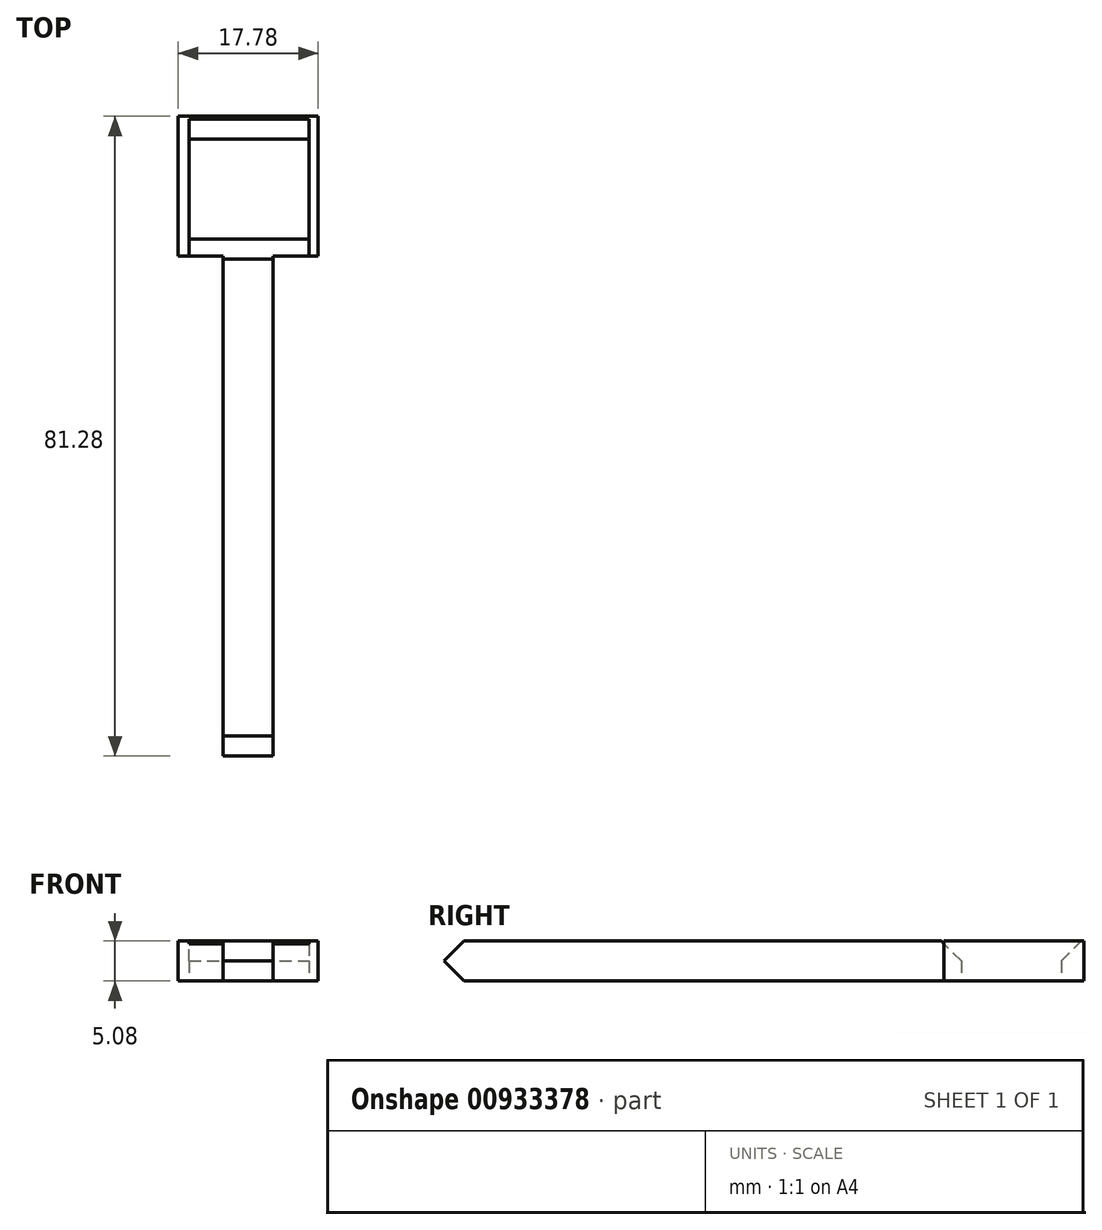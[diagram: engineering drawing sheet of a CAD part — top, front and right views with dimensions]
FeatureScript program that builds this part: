
annotation { "Feature Type Name" : "Feature", "Feature Type Description" : "" }
export const myFeature = defineFeature(function(context is Context, id is Id, definition is map)
    precondition{}
    {
        {
            var Q0;
            Q0=qCreatedBy(makeId("Top.planeOp"),FACE);
            var sketch = newSketch(context, id + "F0", { "sketchPlane" : qUnion([Q0])});
            skLineSegment(sketch, "E0.bottom", {"start": v(-37.97, 21.15) * mm, "end": v(-31.62, 21.15) * mm});
            skLineSegment(sketch, "E0.top", {"start": v(-37.97, -42.35) * mm, "end": v(-31.62, -42.35) * mm});
            skLineSegment(sketch, "E0.left", {"start": v(-37.97, 21.15) * mm, "end": v(-37.97, -42.35) * mm});
            skLineSegment(sketch, "E0.right", {"start": v(-31.62, 21.15) * mm, "end": v(-31.62, -42.35) * mm});
            skLineSegment(sketch, "E1", {"start": v(-34.8, 21.15) * mm, "end": v(-43.69, 21.15) * mm});
            skLineSegment(sketch, "E2", {"start": v(-34.8, 21.15) * mm, "end": v(-25.9, 21.15) * mm});
            skLineSegment(sketch, "E3", {"start": v(-43.69, 21.15) * mm, "end": v(-43.69, 38.93) * mm});
            skLineSegment(sketch, "E4", {"start": v(-43.69, 38.93) * mm, "end": v(-25.9, 38.93) * mm});
            skLineSegment(sketch, "E5", {"start": v(-25.9, 38.93) * mm, "end": v(-25.9, 21.15) * mm});
            skLineSegment(sketch, "E6.bottom", {"start": v(-42.3, 23.34) * mm, "end": v(-27.05, 23.34) * mm});
            skLineSegment(sketch, "E6.top", {"start": v(-42.3, 36.04) * mm, "end": v(-27.05, 36.04) * mm});
            skLineSegment(sketch, "E6.left", {"start": v(-42.3, 23.34) * mm, "end": v(-42.3, 36.04) * mm});
            skLineSegment(sketch, "E6.right", {"start": v(-27.05, 23.34) * mm, "end": v(-27.05, 36.04) * mm});
            skSolve(sketch);
        }
        {
            var Q0;
            {var subQ0=sQuery(id+"F0.wireOp",EDGE,"jYGAuy7J-s2xA-IOac-4ksF-dyn8kirWFf4m.top");Q0=makeQuery(id+"F0.imprint","IMPRINT",FACE,{"disambiguationData":[TD([[makeQuery(id+"F0.imprint","IMPRINT",EDGE,{"derivedFrom":subQ0}),1.0]])]});}
            var Q1;
            {var subQ1=sQuery(id+"F0.wireOp",EDGE,"jYGAuy7J-s2xA-IOac-4ksF-dyn8kirWFf4m.bottom");Q1=makeQuery(id+"F0.imprint","IMPRINT",FACE,{"disambiguationData":[TD([[makeQuery(id+"F0.imprint","IMPRINT",EDGE,{"derivedFrom":subQ1}),-1.0]])]});}
            var Q2;
            {var subQ0=sQuery(id+"F0.wireOp",EDGE,"oYpgsEoI-7KYI-oQ71-cIMU-6RjirgvawTcA");Q2=makeQuery(id+"F0.imprint","IMPRINT",FACE,{"disambiguationData":[TD([[makeQuery(id+"F0.imprint","IMPRINT",EDGE,{"derivedFrom":subQ0}),1.0]])]});}
            var Q3;
            {var subQ3=sQuery(id+"F0.wireOp",EDGE,"E1");Q3=makeQuery(id+"F0.imprint","IMPRINT",FACE,{"disambiguationData":[TD([[makeQuery(id+"F0.imprint","IMPRINT",EDGE,{"derivedFrom":subQ3}),-1.0]])]});}
            var Q4;
            Q4=makeQuery(id+"F0.imprint","IMPRINT",FACE,{"disambiguationData":[TD([[makeQuery(id+"F0.imprint","IMPRINT",EDGE,{"derivedFrom":sQuery(id+"F0.wireOp",EDGE,"E0.top")}),1.0]])]});
            extrude(context, id + "F1", {"entities" : qUnion([Q0, Q1, Q2, Q3, Q4]), "depth" : 5.08 * mm, "offsetDistance" : 25.4 * mm});
        }
        {
            var Q0;
            Q0=makeQuery(id+"F1.opExtrude","CAP_EDGE",EDGE,{"disambiguationData":[OSD([sQuery(id+"F0.wireOp",EDGE,"6foblNvt-KqFc-c7Ez-31U3-n3LWfd83iOhp.bottom")])],"isStart":false});
            var Q1;
            Q1=makeQuery(id+"F1.opExtrude","CAP_EDGE",EDGE,{"disambiguationData":[OSD([sQuery(id+"F0.wireOp",EDGE,"6foblNvt-KqFc-c7Ez-31U3-n3LWfd83iOhp.top")])],"isStart":false});
            var Q2;
            Q2=makeQuery(id+"F1.opExtrude","CAP_EDGE",EDGE,{"disambiguationData":[OSD([sQuery(id+"F0.wireOp",EDGE,"E6.top")])],"isStart":false});
            var Q3;
            Q3=makeQuery(id+"F1.opExtrude","CAP_EDGE",EDGE,{"disambiguationData":[OSD([sQuery(id+"F0.wireOp",EDGE,"E6.bottom")])],"isStart":false});
            var Q4;
            Q4=makeQuery(id+"F1.opExtrude","CAP_EDGE",EDGE,{"disambiguationData":[OSD([sQuery(id+"F0.wireOp",EDGE,"E0.top")])],"isStart":false});
            var Q5;
            Q5=makeQuery(id+"F1.opExtrude","CAP_EDGE",EDGE,{"disambiguationData":[OSD([sQuery(id+"F0.wireOp",EDGE,"E0.top")])],"isStart":true});
            chamfer(context, id + "F2", {"entities" : qUnion([Q0, Q1, Q2, Q3, Q4, Q5]), "width" : 2.54 * mm, "tangentPropagation" : true});
        }
    });
